# Revit family: 304_abefdc61eee44fd28d9691cb15a3e2
name_source: partatom
category: Pipe Accessories
units: mm (PartAtom-declared; Revit-internal decimal feet)

## family parameters
Always vertical = Yes
Cut with Voids When Loaded = No
Part Type = Valve - Breaks Into
Round Connector Dimension = Use Diameter
Shared = No
Work Plane-Based = No

## types (9) — shared parameters
A3WP = 112 mm
ACT1 = No
ACT2L = 230 mm
ACT3L = 93 mm
ACT3W = 167 mm
AL2 = 156 mm
CAT0 = Yes
Description = Pressure independent control valve
L2D = 400 mm
L2D_Min = 3048 mm
Manufacturer = Frese A/S
QmdConnectorList = 301;D;302;D
URL = https://www.frese.eu
W2D = 125 mm
magiPartTypeId = 304
magiProductFamilyId = abefdc61eee44fd28d9691cb15a3e2

## per-type parameters (varying)
| type | ACT2 | ACT2H | ACT3 | D | DD | DF2 | H | H1 | H2 | H3 | H4 | H6 | L2 | L3 | L4 | LF | LF2 | LF__ve | R1 | R3 | R4 | magiProductId |
| Frese Optima Compact Low flow PN16, with spring return actuator UP DN125 | Yes | 289 mm | No | 125 mm | No | 135 mm | 747 mm | 203 mm | 101 mm | 34 mm  [stored 0.111549 ft] | 41 mm  [stored 0.134514 ft] | 193 mm | 200 mm | 336 mm | 188 mm | 32 mm  [stored 0.104987 ft] | 16 mm  [stored 0.0524934 ft] | -32 mm  [stored -0.104987 ft] | 100 mm | 70 mm | 70 mm | b81a04b73a1d458c82d107361bed37 |
| Frese Optima Compact Low flow PN16, with spring return actuator UP DN150 | Yes | 289 mm | No | 150 mm | No | 143 mm | 768 mm | 214 mm | 107 mm | 36 mm | 43 mm | 196 mm | 240 mm | 403 mm | 226 mm | 38 mm | 19 mm | -38 mm | 120 mm | 74 mm | 84 mm | 936f4b161848441f885e637f17bf30 |
| Frese Optima Compact Low flow PN16, with spring return actuator UP DN200 | Yes | 289 mm | No | 200 mm | Yes | 190 mm | 840 mm | 380 mm | 209 mm | 15 mm  [stored 0.0492126 ft] | 57 mm | 159 mm | 300 mm | 504 mm | 282 mm | 48 mm  [stored 0.15748 ft] | 24 mm  [stored 0.0787402 ft] | -48 mm  [stored -0.15748 ft] | 235 mm | 99 mm | 165 mm | 5e6c80327cc3464f96a2f4897b6c7a |
| Frese Optima Compact Low flow PN16, with spring return actuator UP DN250 | Yes | 311 mm | No | 250 mm | Yes | 222 mm | 1094 mm | 444 mm | 244 mm | 15 mm  [stored 0.0492126 ft] | 67 mm  [stored 0.219816 ft] | 339 mm | 365 mm | 613 mm | 343 mm | 58 mm | 29 mm  [stored 0.0951444 ft] | -58 mm | 275 mm | 115 mm | 192 mm | 5e3cb91e439a4862bf10c9c9d3ba4d |
| Frese Optima Compact Low flow PN16, with spring return actuator UP DN300 | Yes | 311 mm | No | 300 mm | Yes | 260 mm | 1132 mm | 520 mm | 286 mm | 15 mm  [stored 0.0492126 ft] | 78 mm | 290 mm | 425 mm | 714 mm | 400 mm | 68 mm | 34 mm  [stored 0.111549 ft] | -68 mm  [stored -0.223097 ft] | 360 mm | 135 mm | 252 mm | a7a3dbfd981347488c707593c4e9cd |
| Frese Optima Compact Low flow PN16, with spring return actuator UP DN50 | No | 289 mm | Yes | 50 mm | No | 83 mm | 508 mm | 124 mm | 62 mm  [stored 0.203412 ft] | 21 mm | 25 mm  [stored 0.082021 ft] | 74 mm | 115 mm | 193 mm | 108 mm | 18 mm | 9 mm | -18 mm | 58 mm | 43 mm | 40 mm  [stored 0.131234 ft] | 94f7fc44078d44b1a5a0f1124aff41 |
| Frese Optima Compact Low flow PN16, with spring return actuator UP DN65 | No | 289 mm | Yes | 65 mm | No | 93 mm | 525 mm | 139 mm | 69 mm | 23 mm | 28 mm  [stored 0.0918635 ft] | 68 mm | 145 mm | 244 mm | 136 mm | 23 mm | 12 mm  [stored 0.0393701 ft] | -23 mm | 73 mm | 48 mm  [stored 0.15748 ft] | 51 mm | a5dc9d49ad2645e38299df67c2b2bd |
| Frese Optima Compact Low flow PN16, with spring return actuator UP DN80 | No | 289 mm | Yes | 80 mm | No | 100 mm | 554 mm | 150 mm | 75 mm | 25 mm  [stored 0.082021 ft] | 30 mm  [stored 0.0984252 ft] | 80 mm | 155 mm | 260 mm | 146 mm | 25 mm  [stored 0.082021 ft] | 12 mm  [stored 0.0393701 ft] | -25 mm  [stored -0.082021 ft] | 78 mm | 52 mm  [stored 0.170604 ft] | 54 mm  [stored 0.177165 ft] | 75b090c5e4ed4f799eb57510ddc64a |
| Frese Optima Compact Low flow PN16, with spring return actuator UP DN100 | No | 289 mm | Yes | 100 mm | No | 118 mm | 700 mm | 176 mm | 88 mm | 29 mm  [stored 0.0951444 ft] | 35 mm  [stored 0.114829 ft] | 186 mm | 175 mm | 294 mm | 165 mm | 28 mm  [stored 0.0918635 ft] | 14 mm  [stored 0.0459318 ft] | -28 mm  [stored -0.0918635 ft] | 88 mm | 61 mm  [stored 0.200131 ft] | 61 mm  [stored 0.200131 ft] | 0c0db875c27646c0be21d8ba92beaf |

note: column(s) folded — value = type name in every type: MC Product Code

note: [stored X ft] marks values corroborated as IEEE doubles in the binary element streams (Revit-internal decimal feet)
